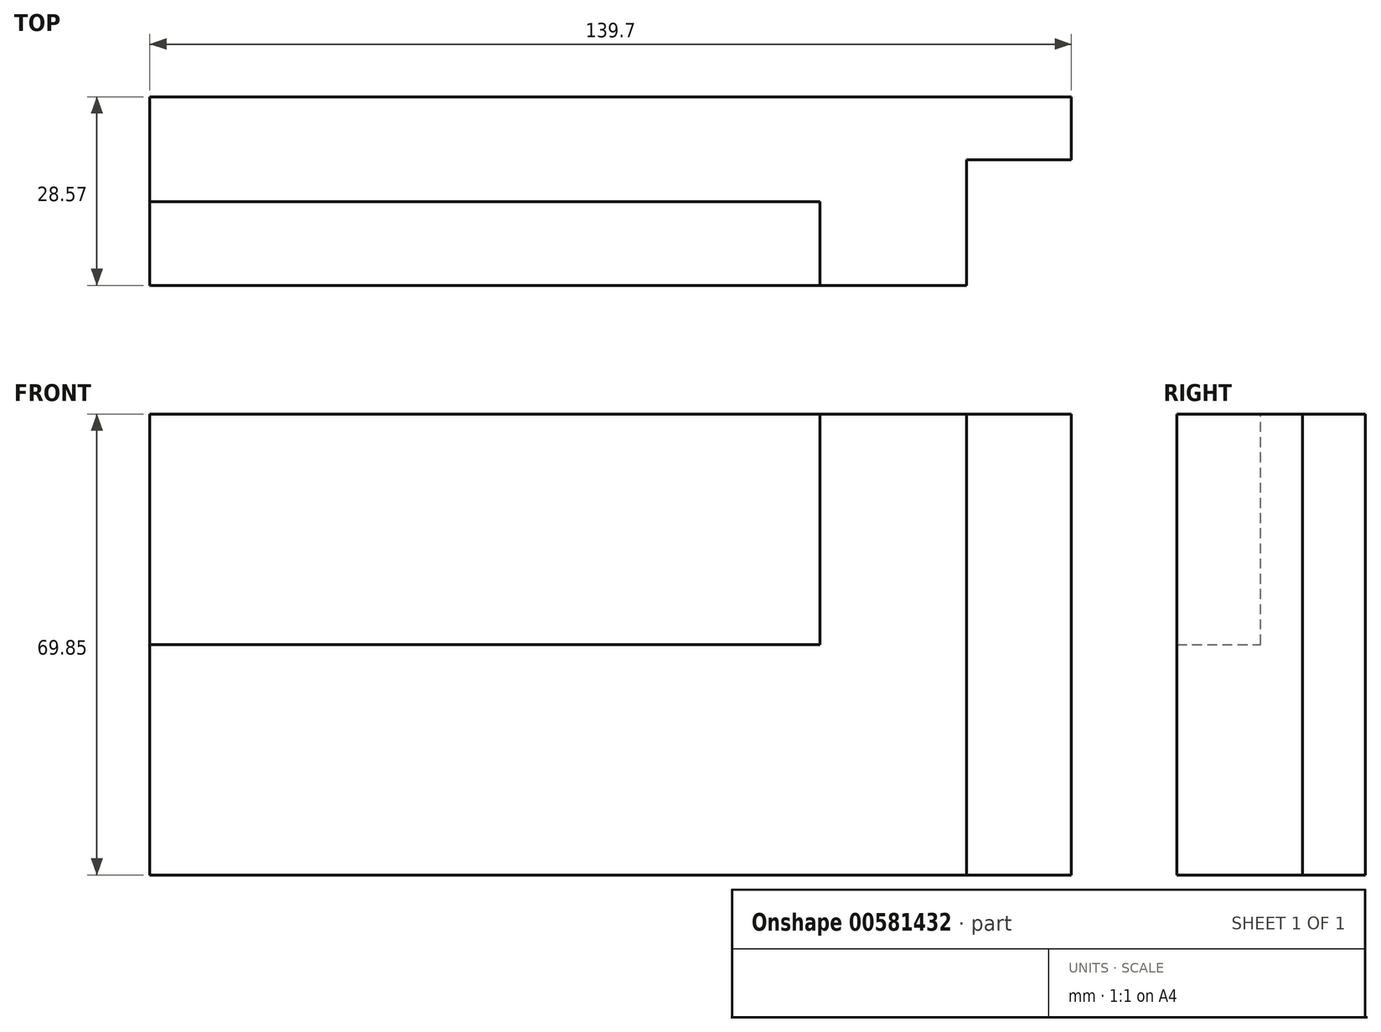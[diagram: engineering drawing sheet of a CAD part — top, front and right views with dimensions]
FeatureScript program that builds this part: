
annotation { "Feature Type Name" : "Feature", "Feature Type Description" : "" }
export const myFeature = defineFeature(function(context is Context, id is Id, definition is map)
    precondition{}
    {
        {
            var Q0;
            Q0=qCreatedBy(makeId("Front.planeOp"),FACE);
            var sketch = newSketch(context, id + "F0", { "sketchPlane" : qUnion([Q0])});
            skLineSegment(sketch, "E0", {"start": v(-64.5, 46.25) * mm, "end": v(-64.5, -23.6) * mm});
            skLineSegment(sketch, "E1", {"start": v(-64.5, -23.6) * mm, "end": v(59.33, -23.6) * mm});
            skLineSegment(sketch, "E2", {"start": v(59.33, -23.6) * mm, "end": v(59.33, 46.25) * mm});
            skLineSegment(sketch, "E3", {"start": v(59.33, 46.25) * mm, "end": v(-64.5, 46.25) * mm});
            skLineSegment(sketch, "E4", {"start": v(-64.5, 11.33) * mm, "end": v(37.1, 11.33) * mm});
            skLineSegment(sketch, "E5", {"start": v(37.1, 11.33) * mm, "end": v(37.1, 46.25) * mm});
            skLineSegment(sketch, "E6", {"start": v(59.33, 46.25) * mm, "end": v(75.2, 46.25) * mm});
            skLineSegment(sketch, "E7", {"start": v(75.2, 46.25) * mm, "end": v(75.2, -23.6) * mm});
            skLineSegment(sketch, "E8", {"start": v(75.2, -23.6) * mm, "end": v(59.33, -23.6) * mm});
            skSolve(sketch);
        }
        {
            var Q0;
            {var subQ3=sQuery(id+"F0.wireOp",EDGE,"E1");Q0=makeQuery(id+"F0.imprint","IMPRINT",FACE,{"disambiguationData":[TD([[makeQuery(id+"F0.imprint","IMPRINT",EDGE,{"derivedFrom":subQ3}),1.0]])]});}
            extrude(context, id + "F1", {"entities" : qUnion([Q0]), "depth" : 28.57 * mm, "offsetDistance" : 25.4 * mm});
        }
        {
            var Q0;
            Q0=qCreatedBy(makeId("Front.planeOp"),FACE);
            var sketch = newSketch(context, id + "F2", { "sketchPlane" : qUnion([Q0])});
            skLineSegment(sketch, "E9.bottom", {"start": v(59.33, -23.6) * mm, "end": v(-64.5, -23.6) * mm});
            skLineSegment(sketch, "E9.top", {"start": v(59.33, 46.25) * mm, "end": v(-64.5, 46.25) * mm});
            skLineSegment(sketch, "E9.left", {"start": v(59.33, -23.6) * mm, "end": v(59.33, 46.25) * mm});
            skLineSegment(sketch, "E9.right", {"start": v(-64.5, -23.6) * mm, "end": v(-64.5, 46.25) * mm});
            skSolve(sketch);
        }
        {
            var Q0;
            Q0=makeQuery(id+"F2.imprint","IMPRINT",FACE,{"disambiguationData":[TD([[makeQuery(id+"F2.imprint","IMPRINT",EDGE,{"derivedFrom":sQuery(id+"F2.wireOp",EDGE,"E9.bottom")}),-1.0]])]});
            extrude(context, id + "F3", {"entities" : qUnion([Q0]), "operationType" : NewBodyOperationType.ADD, "depth" : 15.88 * mm, "offsetDistance" : 25.4 * mm});
        }
        {
            var Q0;
            Q0=qCreatedBy(makeId("Front.planeOp"),FACE);
            var sketch = newSketch(context, id + "F4", { "sketchPlane" : qUnion([Q0])});
            skLineSegment(sketch, "E10.bottom", {"start": v(59.33, 46.25) * mm, "end": v(75.2, 46.25) * mm});
            skLineSegment(sketch, "E10.top", {"start": v(59.33, -23.6) * mm, "end": v(75.2, -23.6) * mm});
            skLineSegment(sketch, "E10.left", {"start": v(59.33, 46.25) * mm, "end": v(59.33, -23.6) * mm});
            skLineSegment(sketch, "E10.right", {"start": v(75.2, 46.25) * mm, "end": v(75.2, -23.6) * mm});
            skSolve(sketch);
        }
        {
            var Q0;
            Q0=makeQuery(id+"F4.imprint","IMPRINT",FACE,{"disambiguationData":[TD([[makeQuery(id+"F4.imprint","IMPRINT",EDGE,{"derivedFrom":sQuery(id+"F4.wireOp",EDGE,"E10.bottom")}),-1.0]])]});
            extrude(context, id + "F5", {"entities" : qUnion([Q0]), "operationType" : NewBodyOperationType.ADD, "depth" : 9.52 * mm, "offsetDistance" : 25.4 * mm});
        }
    });
